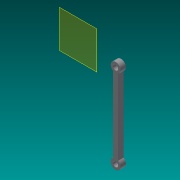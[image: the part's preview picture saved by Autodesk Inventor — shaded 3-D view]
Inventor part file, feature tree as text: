
AUTODESK INVENTOR PART (.ipt)
format: ipt  version: 2013 SP2 (Build 170200200, 200)  size: 101,376 bytes
history: native  units: in
note: dims shown in document units (in); Inventor stores cm internally (conversion verified against a paired STEP export)
features: sheet_metal_op x3, sketch x2, other x2, plane x1
ambient origin geometry x8: Origin, YZ Plane, XZ Plane, XY Plane, X Axis, Y Axis, Z Axis, Center Point
bodies: Solid1 (feature_tree)
feature tree (8):
  sheet_metal_op  "Face1"
  sheet_metal_op  "Face2"
  sketch  "Sketch1"  dims[d1=0.228in]
  other  "Plate1"
  plane  "Work Plane2"
  sketch  "Sketch2"  dims[d2=0.125in d3=0.125in d4=0.125in d5=0.0625in d6=0.25in d7=0.125in]
  other  "Plate2"
  sheet_metal_op  "Bend1"
